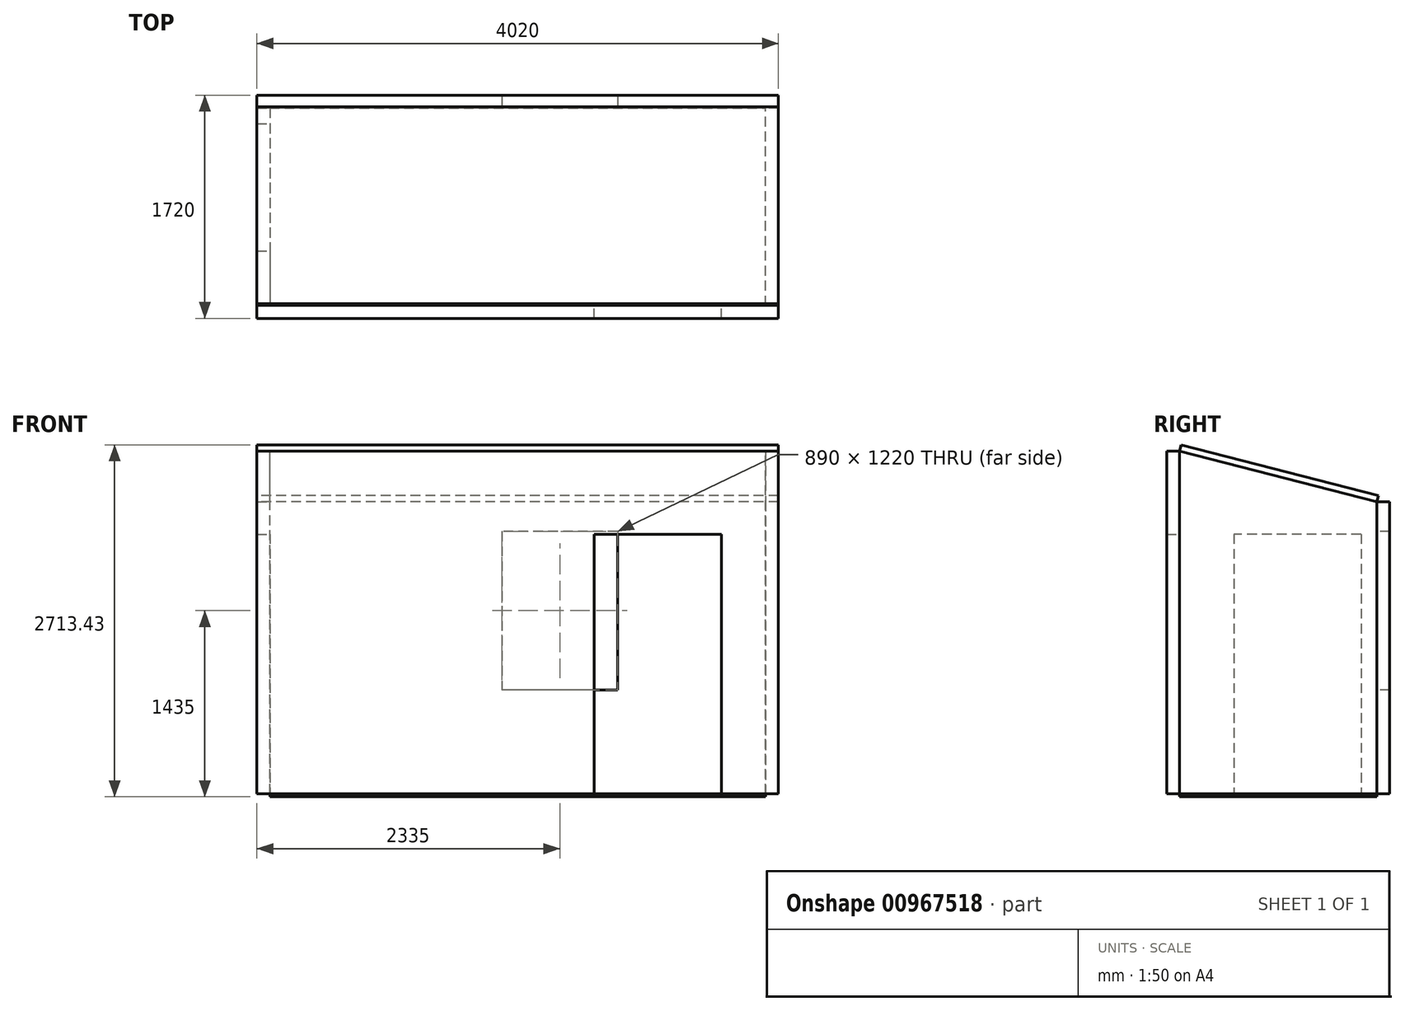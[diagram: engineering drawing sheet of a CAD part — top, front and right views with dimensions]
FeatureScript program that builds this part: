
annotation { "Feature Type Name" : "Feature", "Feature Type Description" : "" }
export const myFeature = defineFeature(function(context is Context, id is Id, definition is map)
    precondition{}
    {
        {
            var Q0;
            Q0=qCreatedBy(makeId("Top.planeOp"),FACE);
            var sketch = newSketch(context, id + "F0", { "sketchPlane" : qUnion([Q0])});
            skLineSegment(sketch, "E0.bottom", {"start": v(0, 0) * mm, "end": v(3820, 0) * mm});
            skLineSegment(sketch, "E0.top", {"start": v(0, 1520) * mm, "end": v(3820, 1520) * mm});
            skLineSegment(sketch, "E0.left", {"start": v(0, 0) * mm, "end": v(0, 1520) * mm});
            skLineSegment(sketch, "E0.right", {"start": v(3820, 0) * mm, "end": v(3820, 1520) * mm});
            skLineSegment(sketch, "E1.bottom", {"start": v(2500, 0) * mm, "end": v(3480, 0) * mm});
            skLineSegment(sketch, "E1.top", {"start": v(2500, -100) * mm, "end": v(3480, -100) * mm});
            skLineSegment(sketch, "E1.left", {"start": v(2500, 0) * mm, "end": v(2500, -100) * mm});
            skLineSegment(sketch, "E1.right", {"start": v(3480, 0) * mm, "end": v(3480, -100) * mm});
            skLineSegment(sketch, "E2.bottom", {"start": v(1790, 1520) * mm, "end": v(2680, 1520) * mm});
            skLineSegment(sketch, "E2.top", {"start": v(1790, 1620) * mm, "end": v(2680, 1620) * mm});
            skLineSegment(sketch, "E2.left", {"start": v(1790, 1520) * mm, "end": v(1790, 1620) * mm});
            skLineSegment(sketch, "E2.right", {"start": v(2680, 1520) * mm, "end": v(2680, 1620) * mm});
            skLineSegment(sketch, "E3.bottom", {"start": v(-100, 1400) * mm, "end": v(0, 1400) * mm});
            skLineSegment(sketch, "E3.top", {"start": v(-100, 420) * mm, "end": v(0, 420) * mm});
            skLineSegment(sketch, "E3.left", {"start": v(-100, 1400) * mm, "end": v(-100, 420) * mm});
            skLineSegment(sketch, "E3.right", {"start": v(0, 1400) * mm, "end": v(0, 420) * mm});
            skSolve(sketch);
        }
        {
            var Q0;
            {var subQ4=sQuery(id+"F0.wireOp",EDGE,"E0.right");Q0=makeQuery(id+"F0.imprint","IMPRINT",FACE,{"disambiguationData":[TD([[makeQuery(id+"F0.imprint","IMPRINT",EDGE,{"derivedFrom":subQ4}),1.0]])]});}
            extrude(context, id + "F1", {"entities" : qUnion([Q0]), "oppositeDirection" : true, "depth" : 25 * mm, "offsetDistance" : 25 * mm});
        }
        {
            var Q0;
            Q0=sQuery(id+"F0.wireOp",EDGE,"E0.top");
            cPlane(context, id + "F2", {"entities" : qUnion([Q0]), "cplaneType" : CPlaneType.LINE_ANGLE, "offset" : 25 * mm, "angle" : 0 * degree, "width" : 150 * mm, "height" : 150 * mm});
        }
        {
            var Q0;
            Q0=sQuery(id+"F0.wireOp",EDGE,"E0.right");
            cPlane(context, id + "F3", {"entities" : qUnion([Q0]), "cplaneType" : CPlaneType.LINE_ANGLE, "offset" : 25 * mm, "angle" : 90 * degree, "width" : 150 * mm, "height" : 150 * mm});
        }
        {
            var Q0;
            Q0=qCreatedBy(makeId("Right.planeOp"),FACE);
            var sketch = newSketch(context, id + "F4", { "sketchPlane" : qUnion([Q0])});
            skLineSegment(sketch, "E4.bottom", {"start": v(1520, 0) * mm, "end": v(0, 0) * mm});
            skLineSegment(sketch, "E4.top", {"start": v(1520, 2250) * mm, "end": v(0, 2640) * mm});
            skLineSegment(sketch, "E4.left", {"start": v(1520, 0) * mm, "end": v(1520, 2250) * mm});
            skLineSegment(sketch, "E4.right", {"start": v(0, 0) * mm, "end": v(0, 2640) * mm});
            skLineSegment(sketch, "E5.bottom", {"start": v(1400, 2000) * mm, "end": v(420, 2000) * mm});
            skLineSegment(sketch, "E5.top", {"start": v(1400, 0) * mm, "end": v(420, 0) * mm});
            skLineSegment(sketch, "E5.left", {"start": v(1400, 2000) * mm, "end": v(1400, 0) * mm});
            skLineSegment(sketch, "E5.right", {"start": v(420, 2000) * mm, "end": v(420, 0) * mm});
            skSolve(sketch);
        }
        {
            var Q0;
            Q0=makeQuery(id+"F4.imprint","IMPRINT",FACE,{"disambiguationData":[TD([[makeQuery(id+"F4.imprint","IMPRINT",EDGE,{"derivedFrom":sQuery(id+"F4.wireOp",EDGE,"E4.top")}),1.0]])]});
            extrude(context, id + "F5", {"entities" : qUnion([Q0]), "oppositeDirection" : true, "depth" : 100 * mm, "offsetDistance" : 25 * mm});
        }
        {
            var Q0;
            Q0=qCreatedBy(id+"F3.planeOp",FACE);
            var sketch = newSketch(context, id + "F6", { "sketchPlane" : qUnion([Q0])});
            skLineSegment(sketch, "E6", {"start": v(0, 0) * mm, "end": v(0, 2640) * mm});
            skLineSegment(sketch, "E7", {"start": v(0, 2640) * mm, "end": v(1520, 2250) * mm});
            skLineSegment(sketch, "E8", {"start": v(1520, 2250) * mm, "end": v(1520, 0) * mm});
            skLineSegment(sketch, "E9", {"start": v(1520, 0) * mm, "end": v(0, 0) * mm});
            skSolve(sketch);
        }
        {
            var Q0;
            Q0 = qSketchRegion(id + "F6", true);
            extrude(context, id + "F7", {"entities" : qUnion([Q0]), "depth" : 100 * mm, "offsetDistance" : 25 * mm});
        }
        {
            var Q0;
            Q0=qCreatedBy(makeId("Front.planeOp"),FACE);
            var sketch = newSketch(context, id + "F8", { "sketchPlane" : qUnion([Q0])});
            skLineSegment(sketch, "E10.bottom", {"start": v(-100, 2640) * mm, "end": v(3920, 2640) * mm});
            skLineSegment(sketch, "E10.top", {"start": v(-100, 0) * mm, "end": v(3920, 0) * mm});
            skLineSegment(sketch, "E10.left", {"start": v(-100, 2640) * mm, "end": v(-100, 0) * mm});
            skLineSegment(sketch, "E10.right", {"start": v(3920, 2640) * mm, "end": v(3920, 0) * mm});
            skLineSegment(sketch, "E11.bottom", {"start": v(2500, 2000) * mm, "end": v(3480, 2000) * mm});
            skLineSegment(sketch, "E11.top", {"start": v(2500, 0) * mm, "end": v(3480, 0) * mm});
            skLineSegment(sketch, "E11.left", {"start": v(2500, 2000) * mm, "end": v(2500, 0) * mm});
            skLineSegment(sketch, "E11.right", {"start": v(3480, 2000) * mm, "end": v(3480, 0) * mm});
            skSolve(sketch);
        }
        {
            var Q0;
            Q0=makeQuery(id+"F8.imprint","IMPRINT",FACE,{"disambiguationData":[TD([[makeQuery(id+"F8.imprint","IMPRINT",EDGE,{"derivedFrom":sQuery(id+"F8.wireOp",EDGE,"E10.bottom")}),-1.0]])]});
            extrude(context, id + "F9", {"entities" : qUnion([Q0]), "depth" : 100 * mm, "offsetDistance" : 25 * mm});
        }
        {
            var Q0;
            Q0=qCreatedBy(id+"F2.planeOp",FACE);
            var sketch = newSketch(context, id + "F10", { "sketchPlane" : qUnion([Q0])});
            skLineSegment(sketch, "E12.bottom", {"start": v(-3920, 2250) * mm, "end": v(100, 2250) * mm});
            skLineSegment(sketch, "E12.top", {"start": v(-3920, 0) * mm, "end": v(100, 0) * mm});
            skLineSegment(sketch, "E12.left", {"start": v(-3920, 2250) * mm, "end": v(-3920, 0) * mm});
            skLineSegment(sketch, "E12.right", {"start": v(100, 2250) * mm, "end": v(100, 0) * mm});
            skLineSegment(sketch, "E13.bottom", {"start": v(-2680, 2020) * mm, "end": v(-1790, 2020) * mm});
            skLineSegment(sketch, "E13.top", {"start": v(-2680, 800) * mm, "end": v(-1790, 800) * mm});
            skLineSegment(sketch, "E13.left", {"start": v(-2680, 2020) * mm, "end": v(-2680, 800) * mm});
            skLineSegment(sketch, "E13.right", {"start": v(-1790, 2020) * mm, "end": v(-1790, 800) * mm});
            skSolve(sketch);
        }
        {
            var Q0;
            Q0 = qSketchRegion(id + "F10", true);
            extrude(context, id + "F11", {"entities" : qUnion([Q0]), "depth" : 100 * mm, "offsetDistance" : 25 * mm});
        }
        {
            var Q0;
            Q0=makeQuery(id+"F5.opExtrude","CAP_FACE",FACE,{"disambiguationData":[OSD([sQuery(id+"F4.wireOp",EDGE,"E4.bottom"),sQuery(id+"F4.wireOp",EDGE,"E4.top"),sQuery(id+"F4.wireOp",EDGE,"E4.left"),sQuery(id+"F4.wireOp",EDGE,"E4.right"),sQuery(id+"F4.wireOp",EDGE,"E5.bottom"),sQuery(id+"F4.wireOp",EDGE,"E5.left"),sQuery(id+"F4.wireOp",EDGE,"E5.right")])],"isStart":false});
            var sketch = newSketch(context, id + "F12", { "sketchPlane" : qUnion([Q0])});
            skLineSegment(sketch, "E14.bottom", {"start": v(-1532.43, 2298.43) * mm, "end": v(-12.43, 2688.43) * mm});
            skLineSegment(sketch, "E14.top", {"start": v(-1520, 2250) * mm, "end": v(0, 2640) * mm});
            skLineSegment(sketch, "E14.left", {"start": v(-1532.43, 2298.43) * mm, "end": v(-1520, 2250) * mm});
            skLineSegment(sketch, "E14.right", {"start": v(-12.43, 2688.43) * mm, "end": v(0, 2640) * mm});
            skSolve(sketch);
        }
        {
            var Q0;
            Q0 = qSketchRegion(id + "F12", true);
            var Q1;
            Q1=makeQuery(id+"F7.opExtrude","CAP_FACE",FACE,{"disambiguationData":[OSD([sQuery(id+"F6.wireOp",EDGE,"E6"),sQuery(id+"F6.wireOp",EDGE,"E7"),sQuery(id+"F6.wireOp",EDGE,"E8"),sQuery(id+"F6.wireOp",EDGE,"E9")])],"isStart":false});
            extrude(context, id + "F13", {"entities" : qUnion([Q0]), "endBound" : BoundingType.UP_TO_SURFACE, "oppositeDirection" : true, "depth" : 25 * mm, "endBoundEntityFace" : qUnion([Q1]), "offsetDistance" : 25 * mm});
        }
    });
